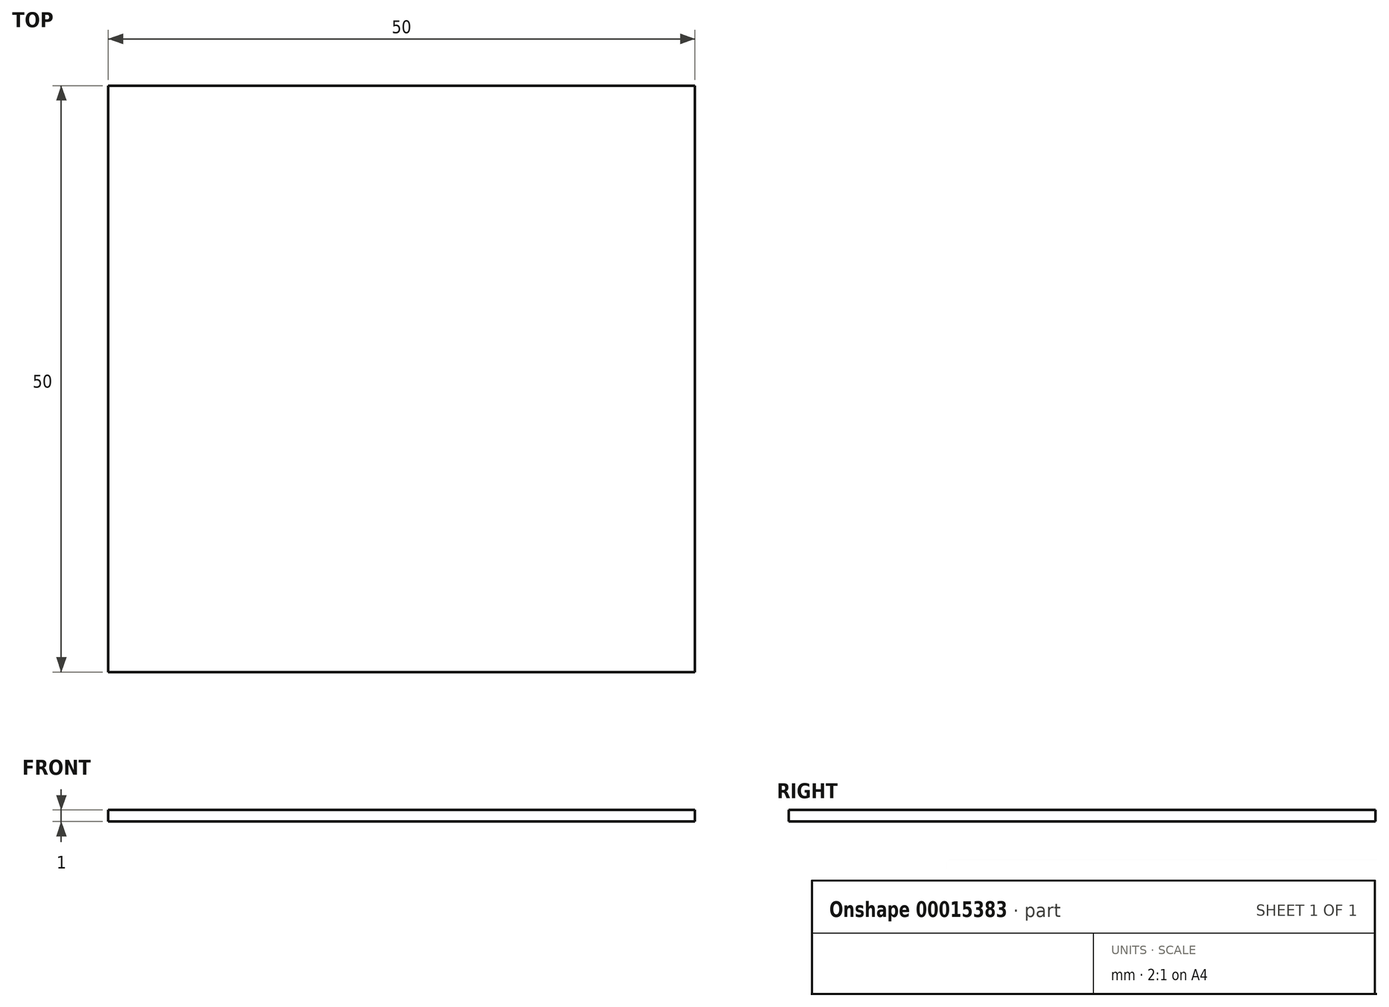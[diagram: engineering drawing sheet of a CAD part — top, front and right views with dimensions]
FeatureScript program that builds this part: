
annotation { "Feature Type Name" : "Feature", "Feature Type Description" : "" }
export const myFeature = defineFeature(function(context is Context, id is Id, definition is map)
    precondition{}
    {
        {
            var Q0;
            Q0=qCreatedBy(makeId("Top.planeOp"),FACE);
            var sketch = newSketch(context, id + "F0", { "sketchPlane" : qUnion([Q0])});
            skLineSegment(sketch, "E0.bottom", {"start": v(-25, 25) * mm, "end": v(25, 25) * mm});
            skLineSegment(sketch, "E0.top", {"start": v(-25, -25) * mm, "end": v(25, -25) * mm});
            skLineSegment(sketch, "E0.left", {"start": v(-25, 25) * mm, "end": v(-25, -25) * mm});
            skLineSegment(sketch, "E0.right", {"start": v(25, 25) * mm, "end": v(25, -25) * mm});
            skSolve(sketch);
        }
        {
            var Q0;
            Q0=makeQuery(id+"F0.imprint","IMPRINT",FACE,{"disambiguationData":[TD([[makeQuery(id+"F0.imprint","IMPRINT",EDGE,{"derivedFrom":sQuery(id+"F0.wireOp",EDGE,"E0.bottom")}),-1.0]])]});
            extrude(context, id + "F1", {"entities" : qUnion([Q0]), "depth" : 1 * mm});
        }
    });
